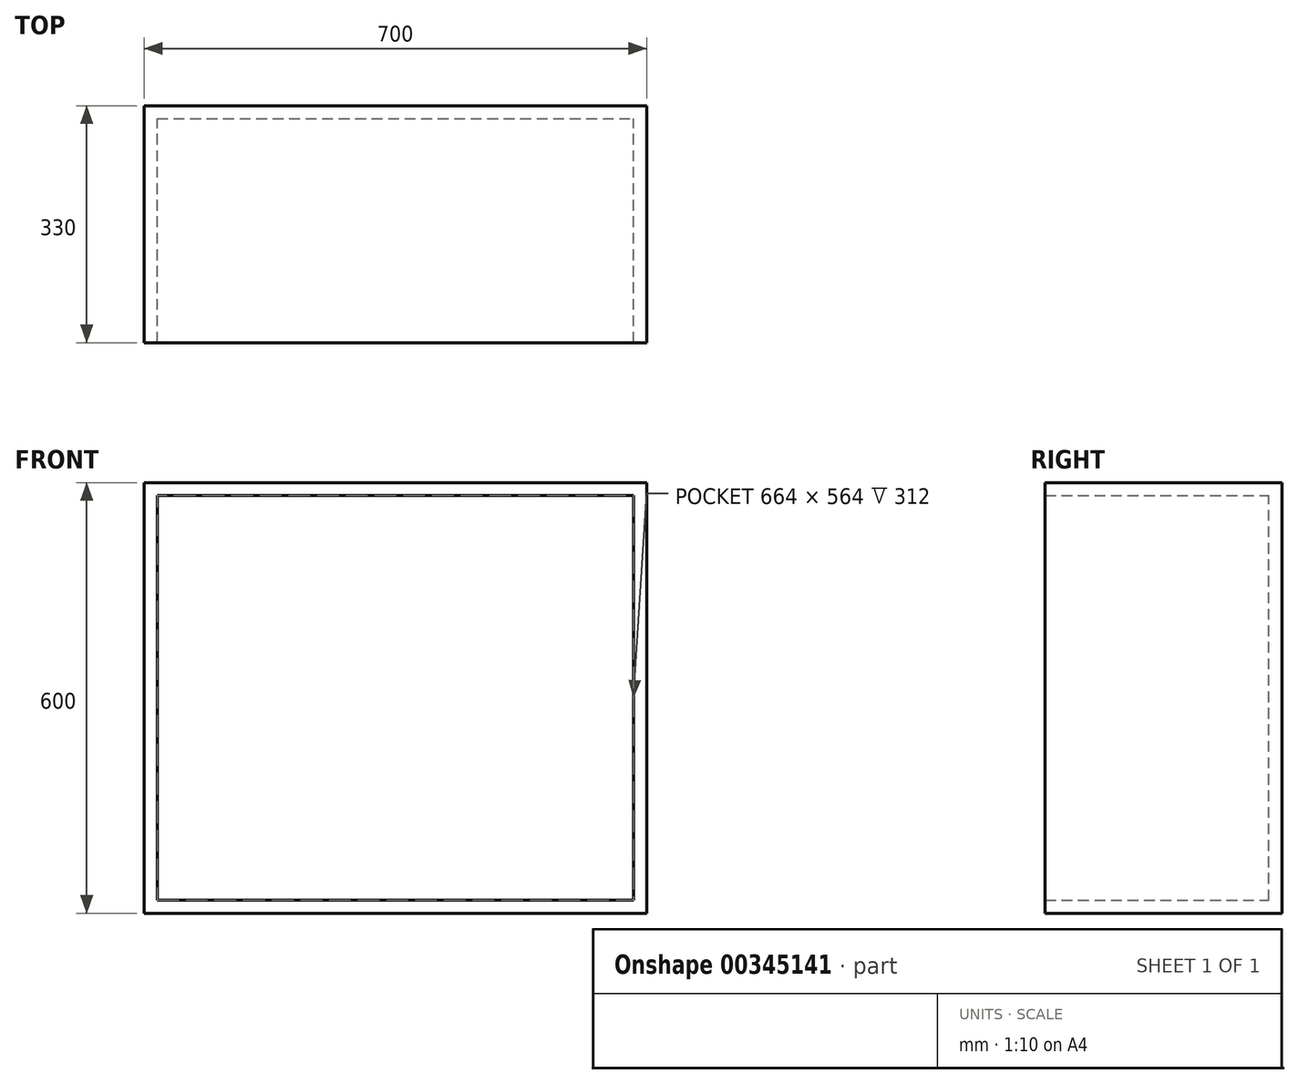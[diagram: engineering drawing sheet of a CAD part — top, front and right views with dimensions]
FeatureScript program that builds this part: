
annotation { "Feature Type Name" : "Feature", "Feature Type Description" : "" }
export const myFeature = defineFeature(function(context is Context, id is Id, definition is map)
    precondition{}
    {
        {
            var Q0;
            Q0=qCreatedBy(makeId("Front.planeOp"),FACE);
            var sketch = newSketch(context, id + "F0", { "sketchPlane" : qUnion([Q0])});
            skLineSegment(sketch, "E0.bottom", {"start": v(0, 0) * mm, "end": v(44.84, 0) * mm});
            skLineSegment(sketch, "E0.top", {"start": v(0, 34.03) * mm, "end": v(44.84, 34.03) * mm});
            skLineSegment(sketch, "E0.left", {"start": v(0, 0) * mm, "end": v(0, 34.03) * mm});
            skLineSegment(sketch, "E0.right", {"start": v(44.84, 0) * mm, "end": v(44.84, 34.03) * mm});
            skSolve(sketch);
        }
        {
            var Q0;
            Q0=makeQuery(id+"F0.imprint","IMPRINT",FACE,{"disambiguationData":[TD([[makeQuery(id+"F0.imprint","IMPRINT",EDGE,{"derivedFrom":sQuery(id+"F0.wireOp",EDGE,"E0.bottom")}),1.0]])]});
            extrude(context, id + "F1", {"entities" : qUnion([Q0]), "depth" : 330 * mm});
        }
        {
            var Q0;
            Q0=makeQuery(id+"F1.opExtrude","SWEPT_FACE",FACE,{"disambiguationData":[OSD([sQuery(id+"F0.wireOp",EDGE,"E0.left")])]});
            extrude(context, id + "F2", {"entities" : qUnion([Q0]), "operationType" : NewBodyOperationType.ADD, "oppositeDirection" : true, "depth" : 900 * mm});
        }
        {
            var Q0;
            {var subQ0=sQuery(id+"F0.wireOp",EDGE,"E0.bottom");Q0=makeQuery(id+"F2.boolean.opBoolean","MERGE",FACE,{"derivedFrom":[makeQuery(id+"F1.opExtrude","SWEPT_FACE",FACE,{"disambiguationData":[OSD([subQ0])]}),makeQuery(id+"F2.opExtrude","SWEPT_FACE",FACE,{"disambiguationData":[OSD([subQ0,sQuery(id+"F0.wireOp",EDGE,"E0.left")])]})]});}
            extrude(context, id + "F3", {"entities" : qUnion([Q0]), "operationType" : NewBodyOperationType.ADD, "oppositeDirection" : true, "depth" : 600 * mm});
        }
        {
            var Q0;
            {var subQ0=sQuery(id+"F0.wireOp",EDGE,"E0.left");var subQ1=sQuery(id+"F0.wireOp",EDGE,"E0.bottom");Q0=makeQuery(id+"F3.boolean.opBoolean","MERGE",FACE,{"derivedFrom":[makeQuery(id+"F2.boolean.opBoolean","MERGE",FACE,{"derivedFrom":[makeQuery(id+"F1.opExtrude","CAP_FACE",FACE,{"disambiguationData":[OSD([subQ1,sQuery(id+"F0.wireOp",EDGE,"E0.top"),subQ0,sQuery(id+"F0.wireOp",EDGE,"E0.right")])],"isStart":false}),makeQuery(id+"F2.opExtrude","SWEPT_FACE",FACE,{"disambiguationData":[OSD([subQ0]),TDD([makeQuery(id+"F1.opExtrude","CAP_EDGE",EDGE,{"disambiguationData":[OSD([subQ0])],"isStart":false})])]})]}),makeQuery(id+"F3.opExtrude","SWEPT_FACE",FACE,{"disambiguationData":[OSD([subQ1,subQ0]),TDD([makeQuery(id+"F2.boolean.opBoolean","MERGE",EDGE,{"derivedFrom":[makeQuery(id+"F1.opExtrude","CAP_EDGE",EDGE,{"disambiguationData":[OSD([subQ1])],"isStart":false}),makeQuery(id+"F2.opExtrude","SWEPT_EDGE",EDGE,{"disambiguationData":[OSD([subQ1,subQ0]),TDD([makeQuery(id+"F1.opExtrude","CAP_VERTEX",VERTEX,{"disambiguationData":[OSD([subQ1,subQ0])],"isStart":false})])]})]})])]})]});}
            shell(context, id + "F4", {"entities" : qUnion([Q0]), "thickness" : 18 * mm});
        }
        {
            var Q0;
            Q0=makeQuery(id+"F1.opExtrude","SWEPT_BODY",BODY,{"disambiguationData":[OSD([sQuery(id+"F0.wireOp",EDGE,"E0.bottom"),sQuery(id+"F0.wireOp",EDGE,"E0.top"),sQuery(id+"F0.wireOp",EDGE,"E0.left"),sQuery(id+"F0.wireOp",EDGE,"E0.right")])]});
            deleteBodies(context, id + "F5", {"entities" : qUnion([Q0])});
        }
        {
            var Q0;
            Q0=qCreatedBy(makeId("Front.planeOp"),FACE);
            var sketch = newSketch(context, id + "F6", { "sketchPlane" : qUnion([Q0])});
            skLineSegment(sketch, "E1.bottom", {"start": v(0, 0) * mm, "end": v(48.9, 0) * mm});
            skLineSegment(sketch, "E1.top", {"start": v(0, 42.58) * mm, "end": v(48.9, 42.58) * mm});
            skLineSegment(sketch, "E1.left", {"start": v(0, 0) * mm, "end": v(0, 42.58) * mm});
            skLineSegment(sketch, "E1.right", {"start": v(48.9, 0) * mm, "end": v(48.9, 42.58) * mm});
            skSolve(sketch);
        }
        {
            var Q0;
            Q0=makeQuery(id+"F6.imprint","IMPRINT",FACE,{"disambiguationData":[TD([[makeQuery(id+"F6.imprint","IMPRINT",EDGE,{"derivedFrom":sQuery(id+"F6.wireOp",EDGE,"E1.bottom")}),1.0]])]});
            extrude(context, id + "F7", {"entities" : qUnion([Q0]), "depth" : 330 * mm});
        }
        {
            var Q0;
            Q0=makeQuery(id+"F7.opExtrude","SWEPT_FACE",FACE,{"disambiguationData":[OSD([sQuery(id+"F6.wireOp",EDGE,"E1.left")])]});
            extrude(context, id + "F8", {"entities" : qUnion([Q0]), "operationType" : NewBodyOperationType.ADD, "oppositeDirection" : true, "depth" : 700 * mm});
        }
        {
            var Q0;
            {var subQ0=sQuery(id+"F6.wireOp",EDGE,"E1.bottom");Q0=makeQuery(id+"F8.boolean.opBoolean","MERGE",FACE,{"derivedFrom":[makeQuery(id+"F7.opExtrude","SWEPT_FACE",FACE,{"disambiguationData":[OSD([subQ0])]}),makeQuery(id+"F8.opExtrude","SWEPT_FACE",FACE,{"disambiguationData":[OSD([subQ0,sQuery(id+"F6.wireOp",EDGE,"E1.left")])]})]});}
            extrude(context, id + "F9", {"entities" : qUnion([Q0]), "operationType" : NewBodyOperationType.ADD, "oppositeDirection" : true, "depth" : 600 * mm});
        }
        {
            var Q0;
            {var subQ0=sQuery(id+"F6.wireOp",EDGE,"E1.left");var subQ1=sQuery(id+"F6.wireOp",EDGE,"E1.bottom");Q0=makeQuery(id+"F9.boolean.opBoolean","MERGE",FACE,{"derivedFrom":[makeQuery(id+"F8.boolean.opBoolean","MERGE",FACE,{"derivedFrom":[makeQuery(id+"F7.opExtrude","CAP_FACE",FACE,{"disambiguationData":[OSD([subQ1,sQuery(id+"F6.wireOp",EDGE,"E1.top"),subQ0,sQuery(id+"F6.wireOp",EDGE,"E1.right")])],"isStart":false}),makeQuery(id+"F8.opExtrude","SWEPT_FACE",FACE,{"disambiguationData":[OSD([subQ0]),TDD([makeQuery(id+"F7.opExtrude","CAP_EDGE",EDGE,{"disambiguationData":[OSD([subQ0])],"isStart":false})])]})]}),makeQuery(id+"F9.opExtrude","SWEPT_FACE",FACE,{"disambiguationData":[OSD([subQ1,subQ0]),TDD([makeQuery(id+"F8.boolean.opBoolean","MERGE",EDGE,{"derivedFrom":[makeQuery(id+"F7.opExtrude","CAP_EDGE",EDGE,{"disambiguationData":[OSD([subQ1])],"isStart":false}),makeQuery(id+"F8.opExtrude","SWEPT_EDGE",EDGE,{"disambiguationData":[OSD([subQ1,subQ0]),TDD([makeQuery(id+"F7.opExtrude","CAP_VERTEX",VERTEX,{"disambiguationData":[OSD([subQ1,subQ0])],"isStart":false})])]})]})])]})]});}
            shell(context, id + "F10", {"entities" : qUnion([Q0]), "thickness" : 18 * mm});
        }
    });
